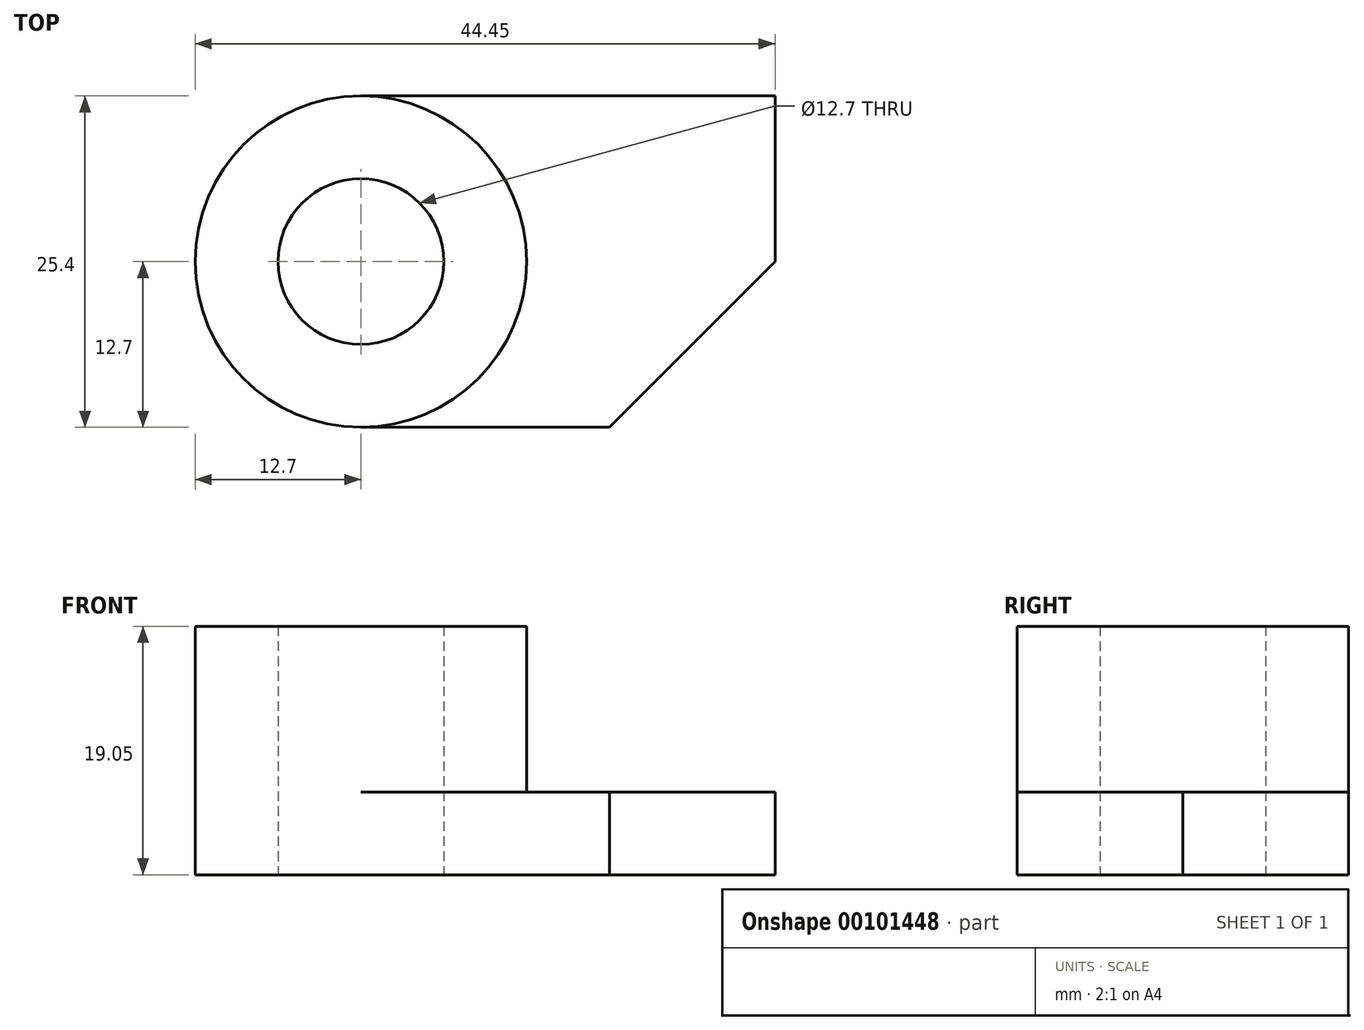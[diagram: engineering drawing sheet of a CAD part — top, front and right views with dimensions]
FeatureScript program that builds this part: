
annotation { "Feature Type Name" : "Feature", "Feature Type Description" : "" }
export const myFeature = defineFeature(function(context is Context, id is Id, definition is map)
    precondition{}
    {
        {
            var Q0;
            Q0=qCreatedBy(makeId("Top.planeOp"),FACE);
            var sketch = newSketch(context, id + "F0", { "sketchPlane" : qUnion([Q0])});
            skLineSegment(sketch, "E0", {"start": v(0, 0) * mm, "end": v(31.75, 0) * mm});
            skLineSegment(sketch, "E1", {"start": v(31.75, 0) * mm, "end": v(31.75, -12.7) * mm});
            skLineSegment(sketch, "E2", {"start": v(31.75, -12.7) * mm, "end": v(19.05, -25.4) * mm});
            skLineSegment(sketch, "E3", {"start": v(19.05, -25.4) * mm, "end": v(0, -25.4) * mm});
            skArc(sketch, "E4", {"start": v(0, 0) * mm, "mid": v(-12.7, -12.7) * mm, "end": v(0, -25.4) * mm});
            skCircle(sketch, "E5", {"center": v(0, -12.7) * mm, "radius": 6.35 * mm});
            skSolve(sketch);
        }
        {
            var Q0;
            Q0 = qSketchRegion(id + "F0", true);
            extrude(context, id + "F1", {"entities" : qUnion([Q0]), "depth" : 6.35 * mm});
        }
        {
            var Q0;
            Q0=makeQuery(id+"F1.opExtrude","CAP_FACE",FACE,{"disambiguationData":[OSD([sQuery(id+"F0.wireOp",EDGE,"E0"),sQuery(id+"F0.wireOp",EDGE,"E1"),sQuery(id+"F0.wireOp",EDGE,"E2"),sQuery(id+"F0.wireOp",EDGE,"E3"),sQuery(id+"F0.wireOp",EDGE,"E4"),sQuery(id+"F0.wireOp",EDGE,"E5")])],"isStart":false});
            var sketch = newSketch(context, id + "F2", { "sketchPlane" : qUnion([Q0])});
            skCircle(sketch, "E6", {"center": v(0, -12.7) * mm, "radius": 6.35 * mm});
            skCircle(sketch, "E7", {"center": v(0, -12.7) * mm, "radius": 12.7 * mm});
            skSolve(sketch);
        }
        {
            var Q0;
            Q0 = qSketchRegion(id + "F2", true);
            extrude(context, id + "F3", {"entities" : qUnion([Q0]), "operationType" : NewBodyOperationType.ADD, "depth" : 12.7 * mm});
        }
    });
